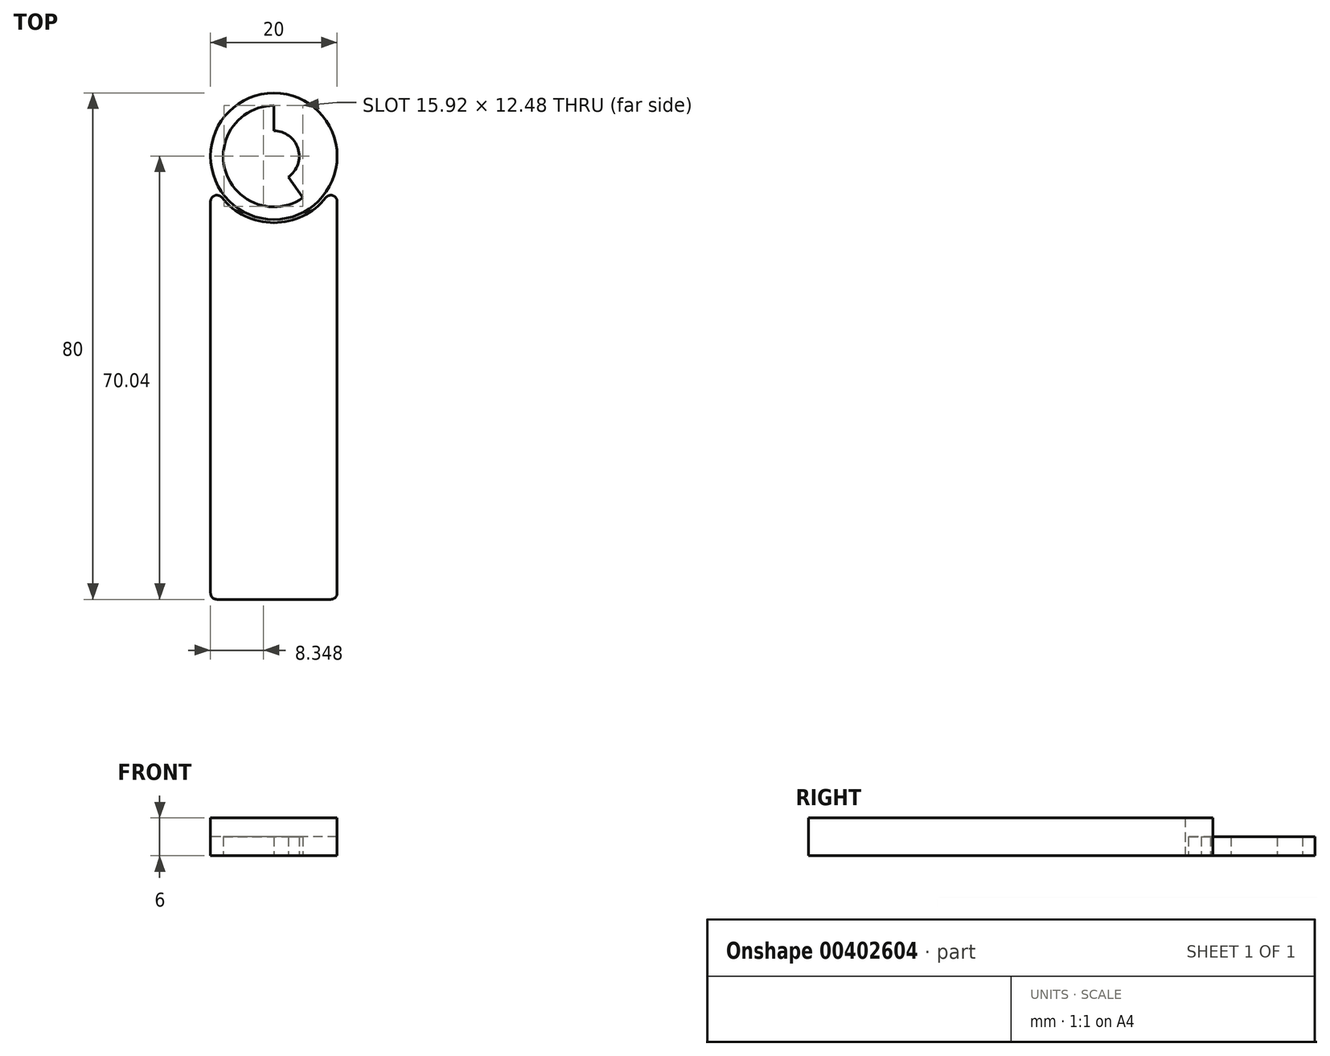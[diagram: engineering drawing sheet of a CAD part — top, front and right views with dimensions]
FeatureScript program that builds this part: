
annotation { "Feature Type Name" : "Feature", "Feature Type Description" : "" }
export const myFeature = defineFeature(function(context is Context, id is Id, definition is map)
    precondition{}
    {
        {
            var Q0;
            Q0=qCreatedBy(makeId("Top.planeOp"),FACE);
            var sketch = newSketch(context, id + "F0", { "sketchPlane" : qUnion([Q0])});
            skCircle(sketch, "E0", {"center": v(0, 0) * mm, "radius": 10 * mm});
            skCircle(sketch, "E1", {"center": v(0, 0) * mm, "radius": 8 * mm});
            skCircle(sketch, "E2", {"center": v(0, 0) * mm, "radius": 1.5 * mm});
            skCircle(sketch, "E3", {"center": v(0, 0) * mm, "radius": 4 * mm});
            skLineSegment(sketch, "E4", {"start": v(0, 4) * mm, "end": v(0, 8) * mm});
            skLineSegment(sketch, "E5.MirrorCS", {"start": v(-4.59, -6.55) * mm, "end": v(0, 0) * mm});
            skLineSegment(sketch, "E6.MirrorCS", {"start": v(4.59, -6.55) * mm, "end": v(0, 0) * mm});
            skLineSegment(sketch, "E7", {"start": v(-10, -70) * mm, "end": v(10, -70) * mm});
            skLineSegment(sketch, "E8", {"start": v(10, -70) * mm, "end": v(10, 0) * mm});
            skLineSegment(sketch, "E9", {"start": v(-10, 0) * mm, "end": v(-10, -70) * mm});
            skArc(sketch, "E10.0", {"start": v(-10, -3.2) * mm, "mid": v(0, -10.5) * mm, "end": v(10, -3.2) * mm});
            skSolve(sketch);
        }
        {
            var Q0;
            Q0=makeQuery(id+"F0.imprint","IMPRINT",FACE,{"disambiguationData":[TD([[makeQuery(id+"F0.imprint","IMPRINT",EDGE,{"derivedFrom":sQuery(id+"F0.wireOp",EDGE,"E7")}),1.0]])]});
            extrude(context, id + "F1", {"entities" : qUnion([Q0]), "depth" : 6 * mm});
        }
        {
            var Q0;
            {var subQ0=sQuery(id+"F0.wireOp",EDGE,"E4");Q0=makeQuery(id+"F0.imprint","IMPRINT",FACE,{"disambiguationData":[TD([[makeQuery(id+"F0.imprint","IMPRINT",EDGE,{"derivedFrom":subQ0}),-1.0]])]});}
            var Q1;
            {var subQ4=sQuery(id+"F0.wireOp",EDGE,"E0");var subQ5=makeQuery(id+"F0.imprint","INTERSECT",VERTEX,{"derivedFrom":[subQ4,sQuery(id+"F0.wireOp",EDGE,"E8")]});Q1=makeQuery(id+"F0.imprint","IMPRINT",FACE,{"disambiguationData":[TD([[makeQuery(id+"F0.imprint","IMPRINT",EDGE,{"disambiguationData":[TD([[subQ5,1.0]])],"derivedFrom":subQ4}),1.0]])]});}
            extrude(context, id + "F2", {"entities" : qUnion([Q0, Q1]), "operationType" : NewBodyOperationType.ADD, "depth" : 3 * mm});
        }
        {
            var Q0;
            {var subQ0=sQuery(id+"F0.wireOp",EDGE,"E0");var subQ1=sQuery(id+"F0.wireOp",EDGE,"E8");Q0=makeQuery(id+"F2.boolean.opBoolean","SPLIT",EDGE,{"disambiguationData":[topologyDisambiguationEdgeConnected([makeQuery(id+"F1.opExtrude","SWEPT_FACE",FACE,{"disambiguationData":[OSD([subQ0])]})])],"derivedFrom":makeQuery(id+"F1.opExtrude","SWEPT_EDGE",EDGE,{"disambiguationData":[OSD([subQ0,subQ1])]})});}
            var Q1;
            {var subQ0=sQuery(id+"F0.wireOp",EDGE,"E0");var subQ1=sQuery(id+"F0.wireOp",EDGE,"E9");Q1=makeQuery(id+"F2.boolean.opBoolean","SPLIT",EDGE,{"disambiguationData":[topologyDisambiguationEdgeConnected([makeQuery(id+"F1.opExtrude","SWEPT_FACE",FACE,{"disambiguationData":[OSD([subQ0])]})])],"derivedFrom":makeQuery(id+"F1.opExtrude","SWEPT_EDGE",EDGE,{"disambiguationData":[OSD([subQ0,subQ1])]})});}
            var Q2;
            Q2=makeQuery(id+"F1.opExtrude","SWEPT_EDGE",EDGE,{"disambiguationData":[OSD([sQuery(id+"F0.wireOp",EDGE,"E7"),sQuery(id+"F0.wireOp",EDGE,"E8")])]});
            var Q3;
            Q3=makeQuery(id+"F1.opExtrude","SWEPT_EDGE",EDGE,{"disambiguationData":[OSD([sQuery(id+"F0.wireOp",EDGE,"E7"),sQuery(id+"F0.wireOp",EDGE,"E9")])]});
            fillet(context, id + "F3", {"entities" : qUnion([Q0, Q1, Q2, Q3]), "radius" : 1 * mm, "tangentPropagation" : true, "allowEdgeOverflow" : false});
        }
    });
